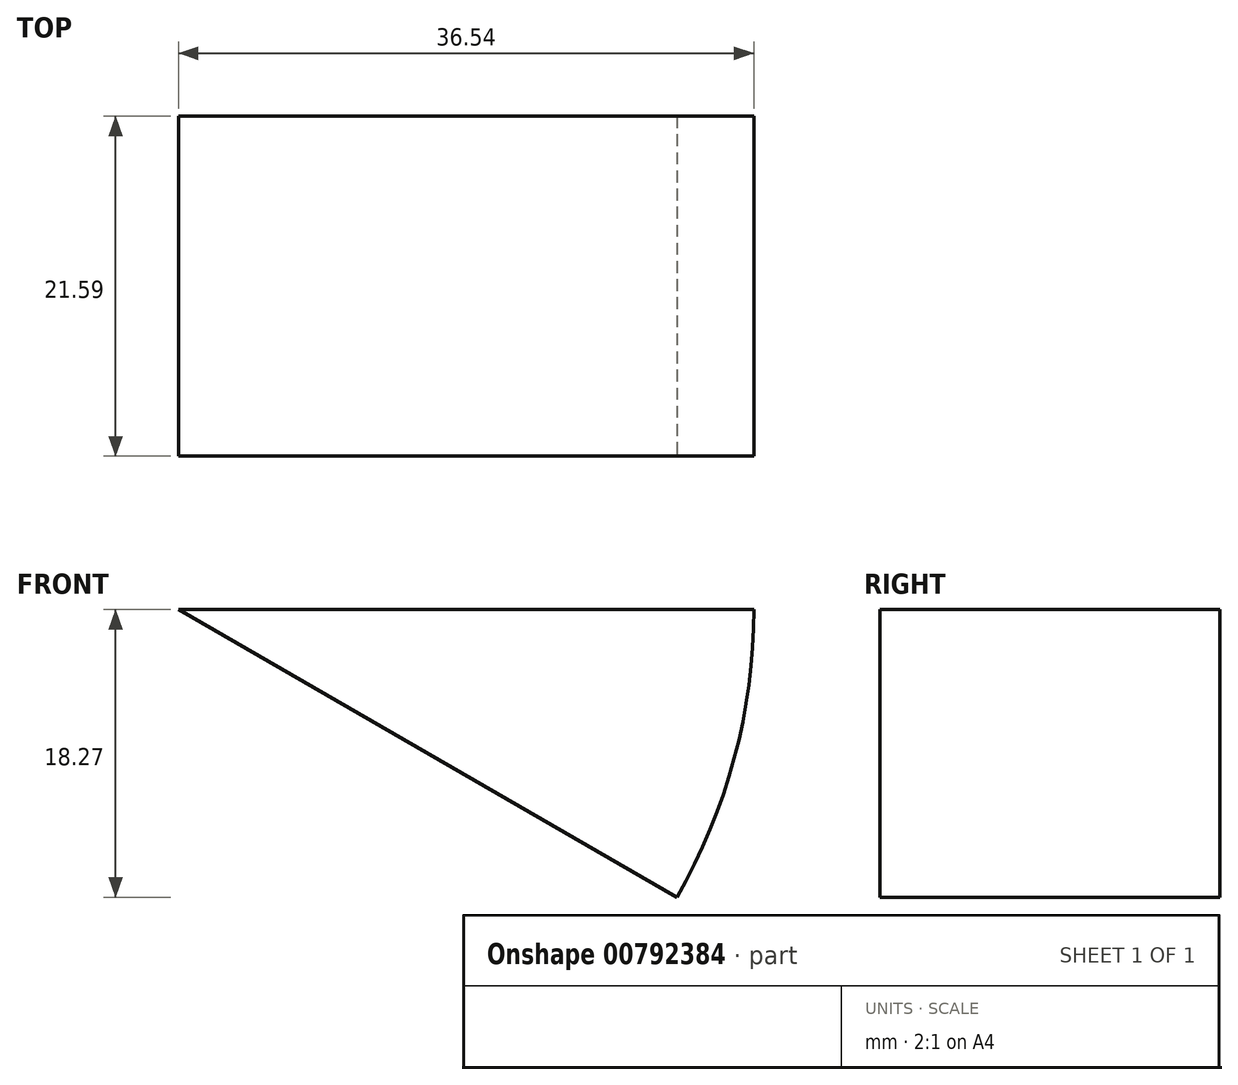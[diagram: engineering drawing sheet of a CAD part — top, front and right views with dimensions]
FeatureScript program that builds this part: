
annotation { "Feature Type Name" : "Feature", "Feature Type Description" : "" }
export const myFeature = defineFeature(function(context is Context, id is Id, definition is map)
    precondition{}
    {
        {
            var Q0;
            Q0=qCreatedBy(makeId("Top.planeOp"),FACE);
            var sketch = newSketch(context, id + "F0", { "sketchPlane" : qUnion([Q0])});
            skCircle(sketch, "E0", {"center": v(-62.28, 52.52) * mm, "radius": 11.18 * mm});
            skLineSegment(sketch, "E1.bottom", {"start": v(23.25, 37.16) * mm, "end": v(59.79, 37.16) * mm});
            skLineSegment(sketch, "E1.top", {"start": v(23.25, 15.57) * mm, "end": v(59.79, 15.57) * mm});
            skLineSegment(sketch, "E1.left", {"start": v(23.25, 37.16) * mm, "end": v(23.25, 15.57) * mm});
            skLineSegment(sketch, "E1.right", {"start": v(59.79, 37.16) * mm, "end": v(59.79, 15.57) * mm});
            skLineSegment(sketch, "E2", {"start": v(-55, -17.45) * mm, "end": v(-20.95, -29.08) * mm});
            skLineSegment(sketch, "E3", {"start": v(-20.95, -29.08) * mm, "end": v(-20.95, -63.13) * mm});
            skLineSegment(sketch, "E4", {"start": v(-20.95, -63.13) * mm, "end": v(-59.98, -69.35) * mm});
            skLineSegment(sketch, "E5", {"start": v(-59.98, -69.35) * mm, "end": v(-55, -17.45) * mm});
            skLineSegment(sketch, "E6", {"start": v(-44.62, -31.99) * mm, "end": v(-50.43, -55.24) * mm});
            skLineSegment(sketch, "E7", {"start": v(-50.43, -55.24) * mm, "end": v(-37.93, -58.36) * mm});
            skLineSegment(sketch, "E8", {"start": v(-37.93, -58.36) * mm, "end": v(-44.62, -31.99) * mm});
            skLineSegment(sketch, "E9", {"start": v(-82.91, 71.7) * mm, "end": v(-82.91, 30.26) * mm, "construction": true});
            skSolve(sketch);
        }
        {
            var Q0;
            Q0=makeQuery(id+"F0.imprint","IMPRINT",FACE,{"disambiguationData":[TD([[makeQuery(id+"F0.imprint","IMPRINT",EDGE,{"derivedFrom":sQuery(id+"F0.wireOp",EDGE,"E1.bottom")}),-1.0]])]});
            var Q1;
            Q1=sQuery(id+"F0.wireOp",EDGE,"E1.left");
            revolve(context, id + "F1", {"surfaceOperationType" : NewSurfaceOperationType.NEW, "entities" : qUnion([Q0]), "axis" : qUnion([Q1]), "revolveType" : RevolveType.ONE_DIRECTION, "oppositeDirection" : true, "angle" : 30 * degree});
        }
    });
